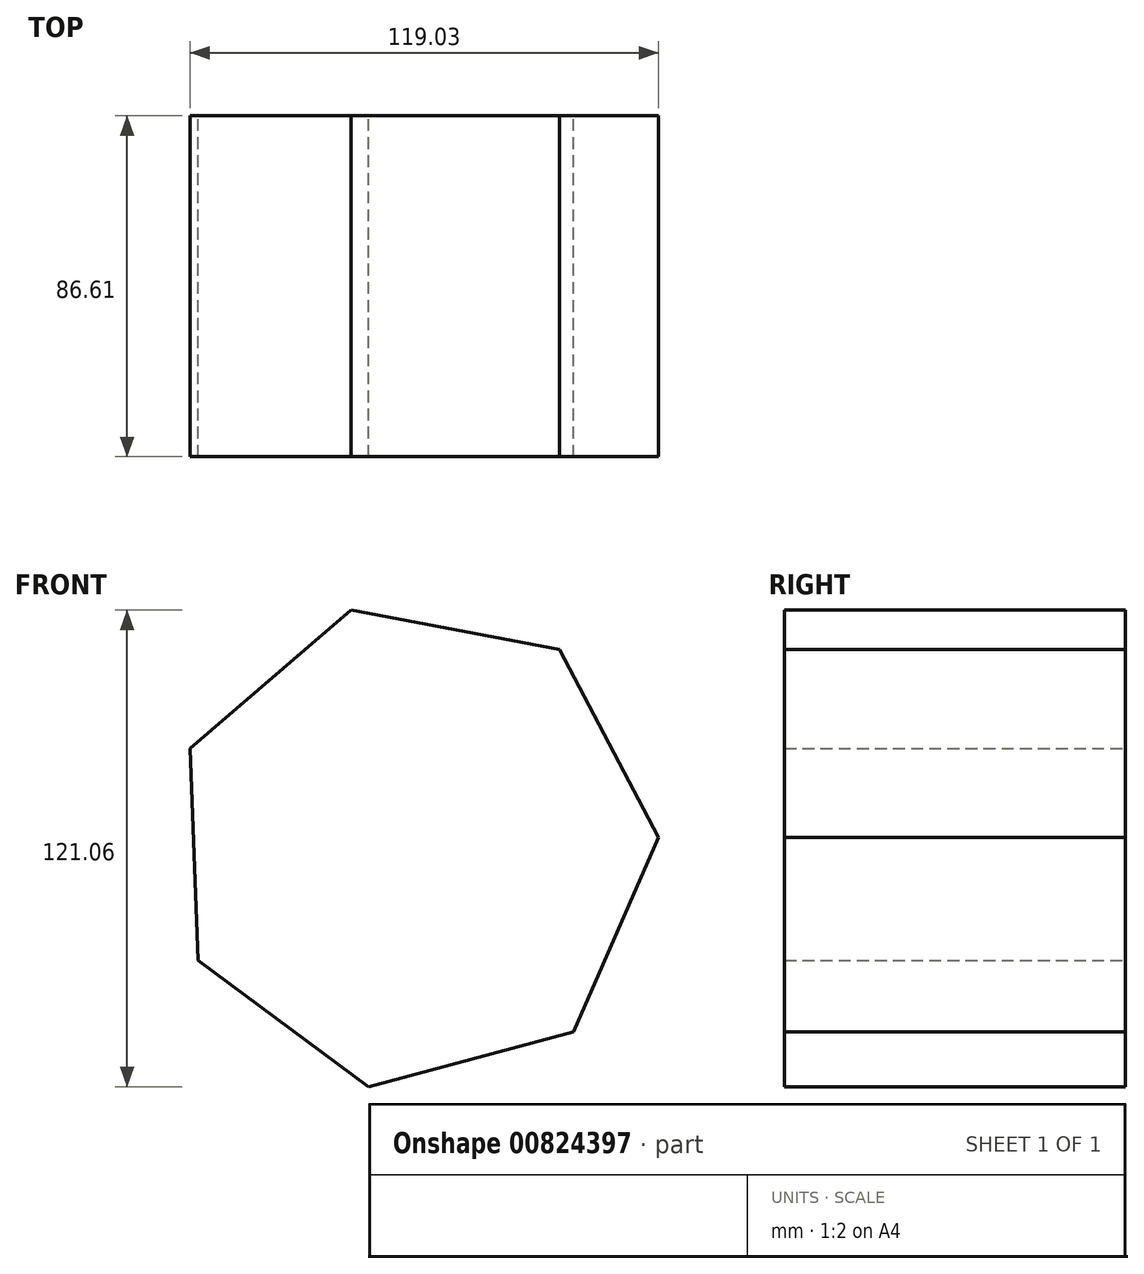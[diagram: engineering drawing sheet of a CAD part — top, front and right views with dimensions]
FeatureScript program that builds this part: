
annotation { "Feature Type Name" : "Feature", "Feature Type Description" : "" }
export const myFeature = defineFeature(function(context is Context, id is Id, definition is map)
    precondition{}
    {
        {
            var Q0;
            Q0=qCreatedBy(makeId("Front.planeOp"),FACE);
            var sketch = newSketch(context, id + "F0", { "sketchPlane" : qUnion([Q0])});
            skCircle(sketch, "E0.cCircle", {"center": v(0, 0) * mm, "radius": 55.98 * mm, "construction": true});
            skLineSegment(sketch, "E0.0", {"start": v(-56.94, 24.87) * mm, "end": v(-16.05, 60.02) * mm});
            skLineSegment(sketch, "E0.1", {"start": v(-16.05, 60.02) * mm, "end": v(36.92, 49.97) * mm});
            skLineSegment(sketch, "E0.2", {"start": v(36.92, 49.97) * mm, "end": v(62.09, 2.3) * mm});
            skLineSegment(sketch, "E0.3", {"start": v(62.09, 2.3) * mm, "end": v(40.5, -47.11) * mm});
            skLineSegment(sketch, "E0.4", {"start": v(40.5, -47.11) * mm, "end": v(-11.58, -61.04) * mm});
            skLineSegment(sketch, "E0.5", {"start": v(-11.58, -61.04) * mm, "end": v(-54.95, -29) * mm});
            skLineSegment(sketch, "E0.6", {"start": v(-54.95, -29) * mm, "end": v(-56.94, 24.87) * mm});
            skPoint(sketch, "E0.0.midPoint", {"position": v(-36.5, 42.45) * mm});
            skSolve(sketch);
        }
        {
            var Q0;
            Q0 = qSketchRegion(id + "F0", true);
            extrude(context, id + "F1", {"entities" : qUnion([Q0]), "depth" : 86.61 * mm, "offsetDistance" : 25.4 * mm});
        }
    });
